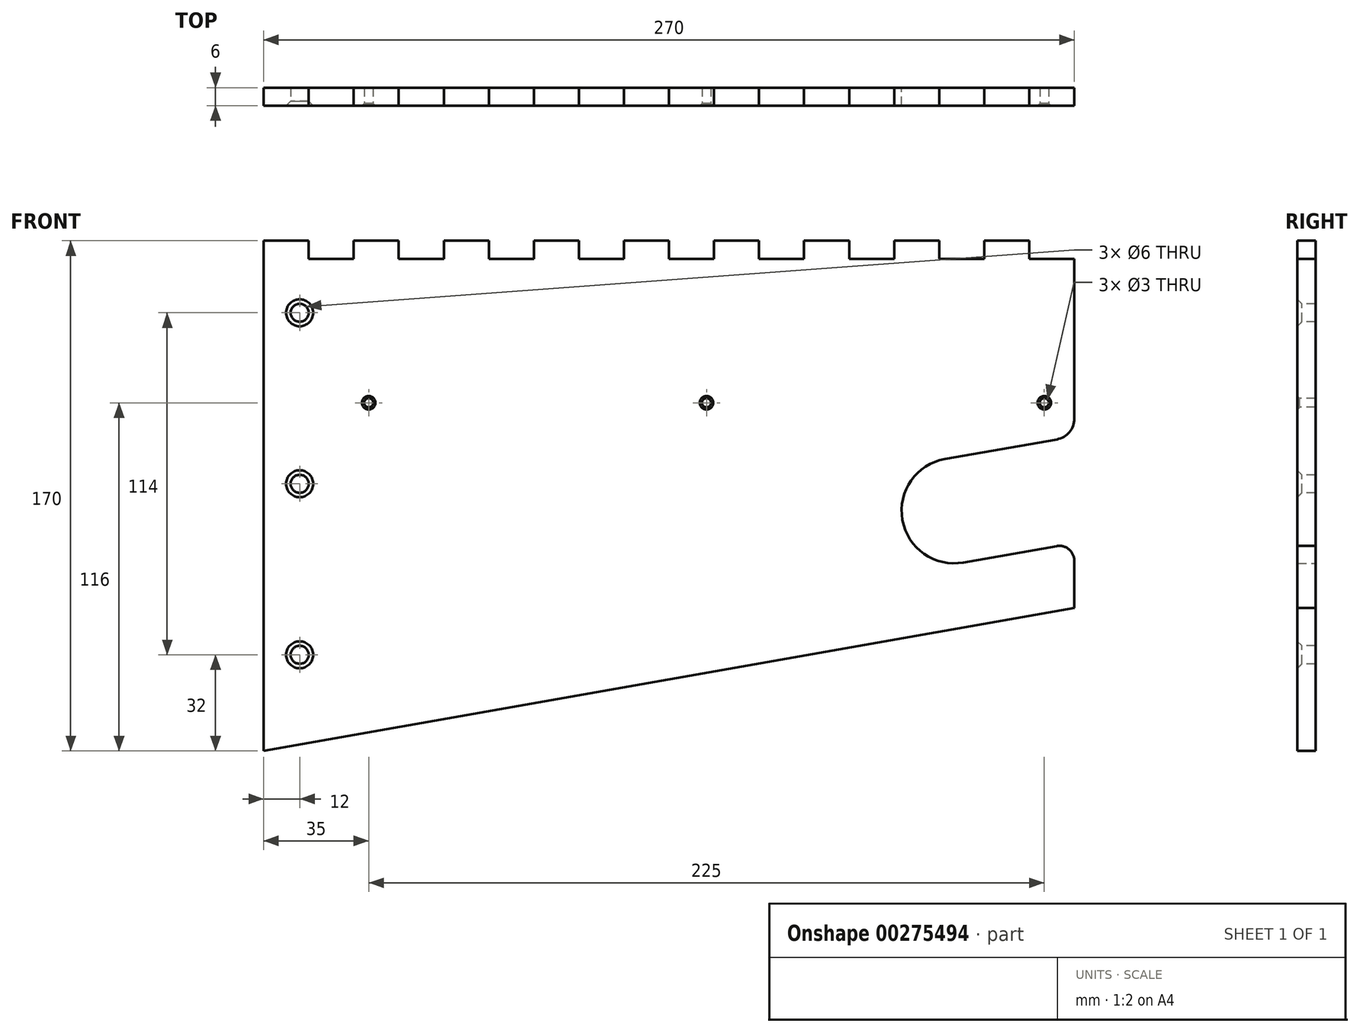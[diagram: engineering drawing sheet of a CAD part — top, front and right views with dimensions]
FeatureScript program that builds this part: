
annotation { "Feature Type Name" : "Feature", "Feature Type Description" : "" }
export const myFeature = defineFeature(function(context is Context, id is Id, definition is map)
    precondition{}
    {
        {
            var Q0;
            Q0=qCreatedBy(makeId("Front.planeOp"),FACE);
            var sketch = newSketch(context, id + "F0", { "sketchPlane" : qUnion([Q0])});
            skLineSegment(sketch, "E0.bottom", {"start": v(0, 0) * mm, "end": v(270, 47.6) * mm});
            skLineSegment(sketch, "E0.top", {"start": v(0, 170) * mm, "end": v(15, 170) * mm});
            skLineSegment(sketch, "E0.left", {"start": v(0, 0) * mm, "end": v(0, 170) * mm});
            skLineSegment(sketch, "E0.right", {"start": v(270, 47.6) * mm, "end": v(270, 63.32) * mm});
            skArc(sketch, "E1", {"start": v(226.96, 97.23) * mm, "mid": v(212.77, 76.96) * mm, "end": v(233.04, 62.77) * mm});
            skLineSegment(sketch, "E2", {"start": v(233.04, 62.77) * mm, "end": v(264.13, 68.25) * mm});
            skLineSegment(sketch, "E3", {"start": v(226.96, 97.23) * mm, "end": v(264.22, 103.8) * mm});
            skLineSegment(sketch, "E4.trimOffspring", {"start": v(270, 110.7) * mm, "end": v(270, 164) * mm});
            skPoint(sketch, "E5.visualSharp", {"position": v(270, 69.28) * mm});
            skArc(sketch, "E5.filletArc", {"start": v(270, 63.32) * mm, "mid": v(268.21, 67.15) * mm, "end": v(264.13, 68.25) * mm});
            skPoint(sketch, "E6.visualSharp", {"position": v(270, 104.82) * mm});
            skArc(sketch, "E6.filletArc", {"start": v(264.22, 103.8) * mm, "mid": v(268.36, 106.2) * mm, "end": v(270, 110.7) * mm});
            skLineSegment(sketch, "E7.top", {"start": v(15, 164) * mm, "end": v(30, 164) * mm});
            skLineSegment(sketch, "E7.left", {"start": v(15, 170) * mm, "end": v(15, 164) * mm});
            skLineSegment(sketch, "E7.right", {"start": v(30, 170) * mm, "end": v(30, 164) * mm});
            skLineSegment(sketch, "E8.1.0.1", {"start": v(45, 170) * mm, "end": v(45, 164) * mm});
            skLineSegment(sketch, "E8.1.0.2", {"start": v(45, 164) * mm, "end": v(60, 164) * mm});
            skLineSegment(sketch, "E8.1.0.3", {"start": v(60, 170) * mm, "end": v(60, 164) * mm});
            skLineSegment(sketch, "E8.2.0.1", {"start": v(75, 170) * mm, "end": v(75, 164) * mm});
            skLineSegment(sketch, "E8.2.0.2", {"start": v(75, 164) * mm, "end": v(90, 164) * mm});
            skLineSegment(sketch, "E8.2.0.3", {"start": v(90, 170) * mm, "end": v(90, 164) * mm});
            skLineSegment(sketch, "E8.3.0.1", {"start": v(105, 170) * mm, "end": v(105, 164) * mm});
            skLineSegment(sketch, "E8.3.0.2", {"start": v(105, 164) * mm, "end": v(120, 164) * mm});
            skLineSegment(sketch, "E8.3.0.3", {"start": v(120, 170) * mm, "end": v(120, 164) * mm});
            skLineSegment(sketch, "E8.4.0.1", {"start": v(135, 170) * mm, "end": v(135, 164) * mm});
            skLineSegment(sketch, "E8.4.0.2", {"start": v(135, 164) * mm, "end": v(150, 164) * mm});
            skLineSegment(sketch, "E8.4.0.3", {"start": v(150, 170) * mm, "end": v(150, 164) * mm});
            skLineSegment(sketch, "E8.5.0.1", {"start": v(165, 170) * mm, "end": v(165, 164) * mm});
            skLineSegment(sketch, "E8.5.0.2", {"start": v(165, 164) * mm, "end": v(180, 164) * mm});
            skLineSegment(sketch, "E8.5.0.3", {"start": v(180, 170) * mm, "end": v(180, 164) * mm});
            skLineSegment(sketch, "E8.6.0.1", {"start": v(195, 170) * mm, "end": v(195, 164) * mm});
            skLineSegment(sketch, "E8.6.0.2", {"start": v(195, 164) * mm, "end": v(210, 164) * mm});
            skLineSegment(sketch, "E8.6.0.3", {"start": v(210, 170) * mm, "end": v(210, 164) * mm});
            skLineSegment(sketch, "E8.7.0.1", {"start": v(225, 170) * mm, "end": v(225, 164) * mm});
            skLineSegment(sketch, "E8.7.0.2", {"start": v(225, 164) * mm, "end": v(240, 164) * mm});
            skLineSegment(sketch, "E8.7.0.3", {"start": v(240, 170) * mm, "end": v(240, 164) * mm});
            skLineSegment(sketch, "E8.8.0.1", {"start": v(255, 170) * mm, "end": v(255, 164) * mm});
            skLineSegment(sketch, "E8.8.0.2", {"start": v(255, 164) * mm, "end": v(270, 164) * mm});
            skLineSegment(sketch, "E8.direction1", {"start": v(30, 170) * mm, "end": v(45, 170) * mm, "construction": true});
            skLineSegment(sketch, "E9.trimOffspring", {"start": v(60, 170) * mm, "end": v(75, 170) * mm});
            skLineSegment(sketch, "E10.trimOffspring", {"start": v(120, 170) * mm, "end": v(135, 170) * mm});
            skLineSegment(sketch, "E11.trimOffspring", {"start": v(150, 170) * mm, "end": v(165, 170) * mm});
            skLineSegment(sketch, "E12.trimOffspring", {"start": v(180, 170) * mm, "end": v(195, 170) * mm});
            skLineSegment(sketch, "E13.trimOffspring", {"start": v(240, 170) * mm, "end": v(255, 170) * mm});
            skLineSegment(sketch, "E14.trimOffspring", {"start": v(210, 170) * mm, "end": v(225, 170) * mm});
            skLineSegment(sketch, "E15.trimOffspring", {"start": v(90, 170) * mm, "end": v(105, 170) * mm});
            skLineSegment(sketch, "E16.trimOffspring", {"start": v(30, 170) * mm, "end": v(45, 170) * mm});
            skSolve(sketch);
        }
        {
            var Q0;
            Q0=makeQuery(id+"F0.imprint","IMPRINT",FACE,{"disambiguationData":[TD([[makeQuery(id+"F0.imprint","IMPRINT",EDGE,{"derivedFrom":sQuery(id+"F0.wireOp",EDGE,"E0.bottom")}),1.0]])]});
            extrude(context, id + "F1", {"entities" : qUnion([Q0]), "depth" : 6 * mm});
        }
        {
            var Q0;
            Q0=makeQuery(id+"F1.opExtrude","CAP_FACE",FACE,{"disambiguationData":[OSD([sQuery(id+"F0.wireOp",EDGE,"E0.bottom"),sQuery(id+"F0.wireOp",EDGE,"E0.top"),sQuery(id+"F0.wireOp",EDGE,"E0.left"),sQuery(id+"F0.wireOp",EDGE,"E0.right"),sQuery(id+"F0.wireOp",EDGE,"E1"),sQuery(id+"F0.wireOp",EDGE,"E2"),sQuery(id+"F0.wireOp",EDGE,"E3"),sQuery(id+"F0.wireOp",EDGE,"E4.trimOffspring"),sQuery(id+"F0.wireOp",EDGE,"E5.filletArc"),sQuery(id+"F0.wireOp",EDGE,"E6.filletArc"),sQuery(id+"F0.wireOp",EDGE,"E7.top"),sQuery(id+"F0.wireOp",EDGE,"E7.left"),sQuery(id+"F0.wireOp",EDGE,"E7.right"),sQuery(id+"F0.wireOp",EDGE,"E8.1.0.1"),sQuery(id+"F0.wireOp",EDGE,"E8.1.0.2"),sQuery(id+"F0.wireOp",EDGE,"E8.1.0.3"),sQuery(id+"F0.wireOp",EDGE,"E8.2.0.1"),sQuery(id+"F0.wireOp",EDGE,"E8.2.0.2"),sQuery(id+"F0.wireOp",EDGE,"E8.2.0.3"),sQuery(id+"F0.wireOp",EDGE,"E8.3.0.1"),sQuery(id+"F0.wireOp",EDGE,"E8.3.0.2"),sQuery(id+"F0.wireOp",EDGE,"E8.3.0.3"),sQuery(id+"F0.wireOp",EDGE,"E8.4.0.1"),sQuery(id+"F0.wireOp",EDGE,"E8.4.0.2"),sQuery(id+"F0.wireOp",EDGE,"E8.4.0.3"),sQuery(id+"F0.wireOp",EDGE,"E8.5.0.1"),sQuery(id+"F0.wireOp",EDGE,"E8.5.0.2"),sQuery(id+"F0.wireOp",EDGE,"E8.5.0.3"),sQuery(id+"F0.wireOp",EDGE,"E8.6.0.1"),sQuery(id+"F0.wireOp",EDGE,"E8.6.0.2"),sQuery(id+"F0.wireOp",EDGE,"E8.6.0.3"),sQuery(id+"F0.wireOp",EDGE,"E8.7.0.1"),sQuery(id+"F0.wireOp",EDGE,"E8.7.0.2"),sQuery(id+"F0.wireOp",EDGE,"E8.7.0.3"),sQuery(id+"F0.wireOp",EDGE,"E8.8.0.1"),sQuery(id+"F0.wireOp",EDGE,"E8.8.0.2"),sQuery(id+"F0.wireOp",EDGE,"E9.trimOffspring"),sQuery(id+"F0.wireOp",EDGE,"E10.trimOffspring"),sQuery(id+"F0.wireOp",EDGE,"E11.trimOffspring"),sQuery(id+"F0.wireOp",EDGE,"E12.trimOffspring"),sQuery(id+"F0.wireOp",EDGE,"E13.trimOffspring"),sQuery(id+"F0.wireOp",EDGE,"E14.trimOffspring"),sQuery(id+"F0.wireOp",EDGE,"E15.trimOffspring"),sQuery(id+"F0.wireOp",EDGE,"E16.trimOffspring")])],"isStart":false});
            var sketch = newSketch(context, id + "F2", { "sketchPlane" : qUnion([Q0])});
            skPoint(sketch, "E17", {"position": v(12, 146) * mm});
            skPoint(sketch, "E18", {"position": v(12, 89) * mm});
            skPoint(sketch, "E19", {"position": v(12, 32) * mm});
            skSolve(sketch);
        }
        {
            var Q0;
            Q0=sQuery(id+"F2.wireOp",VERTEX,"E17");
            var Q1;
            Q1=sQuery(id+"F2.wireOp",VERTEX,"E18");
            var Q2;
            Q2=sQuery(id+"F2.wireOp",VERTEX,"E19");
            var Q3;
            Q3=makeQuery(id+"F1.opExtrude","SWEPT_BODY",BODY,{"disambiguationData":[OSD([sQuery(id+"F0.wireOp",EDGE,"E0.bottom"),sQuery(id+"F0.wireOp",EDGE,"E0.top"),sQuery(id+"F0.wireOp",EDGE,"E0.left"),sQuery(id+"F0.wireOp",EDGE,"E0.right"),sQuery(id+"F0.wireOp",EDGE,"E1"),sQuery(id+"F0.wireOp",EDGE,"E2"),sQuery(id+"F0.wireOp",EDGE,"E3"),sQuery(id+"F0.wireOp",EDGE,"E4.trimOffspring"),sQuery(id+"F0.wireOp",EDGE,"E5.filletArc"),sQuery(id+"F0.wireOp",EDGE,"E6.filletArc"),sQuery(id+"F0.wireOp",EDGE,"E7.top"),sQuery(id+"F0.wireOp",EDGE,"E7.left"),sQuery(id+"F0.wireOp",EDGE,"E7.right"),sQuery(id+"F0.wireOp",EDGE,"E8.1.0.1"),sQuery(id+"F0.wireOp",EDGE,"E8.1.0.2"),sQuery(id+"F0.wireOp",EDGE,"E8.1.0.3"),sQuery(id+"F0.wireOp",EDGE,"E8.2.0.1"),sQuery(id+"F0.wireOp",EDGE,"E8.2.0.2"),sQuery(id+"F0.wireOp",EDGE,"E8.2.0.3"),sQuery(id+"F0.wireOp",EDGE,"E8.3.0.1"),sQuery(id+"F0.wireOp",EDGE,"E8.3.0.2"),sQuery(id+"F0.wireOp",EDGE,"E8.3.0.3"),sQuery(id+"F0.wireOp",EDGE,"E8.4.0.1"),sQuery(id+"F0.wireOp",EDGE,"E8.4.0.2"),sQuery(id+"F0.wireOp",EDGE,"E8.4.0.3"),sQuery(id+"F0.wireOp",EDGE,"E8.5.0.1"),sQuery(id+"F0.wireOp",EDGE,"E8.5.0.2"),sQuery(id+"F0.wireOp",EDGE,"E8.5.0.3"),sQuery(id+"F0.wireOp",EDGE,"E8.6.0.1"),sQuery(id+"F0.wireOp",EDGE,"E8.6.0.2"),sQuery(id+"F0.wireOp",EDGE,"E8.6.0.3"),sQuery(id+"F0.wireOp",EDGE,"E8.7.0.1"),sQuery(id+"F0.wireOp",EDGE,"E8.7.0.2"),sQuery(id+"F0.wireOp",EDGE,"E8.7.0.3"),sQuery(id+"F0.wireOp",EDGE,"E8.8.0.1"),sQuery(id+"F0.wireOp",EDGE,"E8.8.0.2"),sQuery(id+"F0.wireOp",EDGE,"E9.trimOffspring"),sQuery(id+"F0.wireOp",EDGE,"E10.trimOffspring"),sQuery(id+"F0.wireOp",EDGE,"E11.trimOffspring"),sQuery(id+"F0.wireOp",EDGE,"E12.trimOffspring"),sQuery(id+"F0.wireOp",EDGE,"E13.trimOffspring"),sQuery(id+"F0.wireOp",EDGE,"E14.trimOffspring"),sQuery(id+"F0.wireOp",EDGE,"E15.trimOffspring"),sQuery(id+"F0.wireOp",EDGE,"E16.trimOffspring")])]});
            hole(context, id + "F3", {"style" : HoleStyle.C_SINK, "endStyle" : HoleEndStyle.THROUGH, "standardTappedOrClearance" : lookupTablePath({ "standard" : "ISO", "size" : "6", "type" : "Drilled" }), "standardBlindInLast" : lookupTablePath({ "standard" : "ISO", "size" : "6", "type" : "Drilled" }), "holeDiameter" : 6 * mm, "cSinkDiameter" : 9 * mm, "cSinkAngle" : 90 * degree, "tappedDepth" : 12 * mm, "tapClearance" : 3, "locations" : qUnion([Q0, Q1, Q2]), "scope" : qUnion([Q3])});
        }
        {
            var Q0;
            Q0=makeQuery(id+"F1.opExtrude","CAP_FACE",FACE,{"disambiguationData":[OSD([sQuery(id+"F0.wireOp",EDGE,"E0.bottom"),sQuery(id+"F0.wireOp",EDGE,"E0.top"),sQuery(id+"F0.wireOp",EDGE,"E0.left"),sQuery(id+"F0.wireOp",EDGE,"E0.right"),sQuery(id+"F0.wireOp",EDGE,"E1"),sQuery(id+"F0.wireOp",EDGE,"E2"),sQuery(id+"F0.wireOp",EDGE,"E3"),sQuery(id+"F0.wireOp",EDGE,"E4.trimOffspring"),sQuery(id+"F0.wireOp",EDGE,"E5.filletArc"),sQuery(id+"F0.wireOp",EDGE,"E6.filletArc"),sQuery(id+"F0.wireOp",EDGE,"E7.top"),sQuery(id+"F0.wireOp",EDGE,"E7.left"),sQuery(id+"F0.wireOp",EDGE,"E7.right"),sQuery(id+"F0.wireOp",EDGE,"E8.1.0.1"),sQuery(id+"F0.wireOp",EDGE,"E8.1.0.2"),sQuery(id+"F0.wireOp",EDGE,"E8.1.0.3"),sQuery(id+"F0.wireOp",EDGE,"E8.2.0.1"),sQuery(id+"F0.wireOp",EDGE,"E8.2.0.2"),sQuery(id+"F0.wireOp",EDGE,"E8.2.0.3"),sQuery(id+"F0.wireOp",EDGE,"E8.3.0.1"),sQuery(id+"F0.wireOp",EDGE,"E8.3.0.2"),sQuery(id+"F0.wireOp",EDGE,"E8.3.0.3"),sQuery(id+"F0.wireOp",EDGE,"E8.4.0.1"),sQuery(id+"F0.wireOp",EDGE,"E8.4.0.2"),sQuery(id+"F0.wireOp",EDGE,"E8.4.0.3"),sQuery(id+"F0.wireOp",EDGE,"E8.5.0.1"),sQuery(id+"F0.wireOp",EDGE,"E8.5.0.2"),sQuery(id+"F0.wireOp",EDGE,"E8.5.0.3"),sQuery(id+"F0.wireOp",EDGE,"E8.6.0.1"),sQuery(id+"F0.wireOp",EDGE,"E8.6.0.2"),sQuery(id+"F0.wireOp",EDGE,"E8.6.0.3"),sQuery(id+"F0.wireOp",EDGE,"E8.7.0.1"),sQuery(id+"F0.wireOp",EDGE,"E8.7.0.2"),sQuery(id+"F0.wireOp",EDGE,"E8.7.0.3"),sQuery(id+"F0.wireOp",EDGE,"E8.8.0.1"),sQuery(id+"F0.wireOp",EDGE,"E8.8.0.2"),sQuery(id+"F0.wireOp",EDGE,"E9.trimOffspring"),sQuery(id+"F0.wireOp",EDGE,"E10.trimOffspring"),sQuery(id+"F0.wireOp",EDGE,"E11.trimOffspring"),sQuery(id+"F0.wireOp",EDGE,"E12.trimOffspring"),sQuery(id+"F0.wireOp",EDGE,"E13.trimOffspring"),sQuery(id+"F0.wireOp",EDGE,"E14.trimOffspring"),sQuery(id+"F0.wireOp",EDGE,"E15.trimOffspring"),sQuery(id+"F0.wireOp",EDGE,"E16.trimOffspring")])],"isStart":false});
            var sketch = newSketch(context, id + "F4", { "sketchPlane" : qUnion([Q0])});
            skPoint(sketch, "E20", {"position": v(35, 116) * mm});
            skPoint(sketch, "E21", {"position": v(147.5, 116) * mm});
            skPoint(sketch, "E22", {"position": v(260, 116) * mm});
            skSolve(sketch);
        }
        {
            var Q0;
            Q0=sQuery(id+"F4.wireOp",VERTEX,"E20");
            var Q1;
            Q1=sQuery(id+"F4.wireOp",VERTEX,"E21");
            var Q2;
            Q2=sQuery(id+"F4.wireOp",VERTEX,"E22");
            var Q3;
            Q3=makeQuery(id+"F1.opExtrude","SWEPT_BODY",BODY,{"disambiguationData":[OSD([sQuery(id+"F0.wireOp",EDGE,"E0.bottom"),sQuery(id+"F0.wireOp",EDGE,"E0.top"),sQuery(id+"F0.wireOp",EDGE,"E0.left"),sQuery(id+"F0.wireOp",EDGE,"E0.right"),sQuery(id+"F0.wireOp",EDGE,"E1"),sQuery(id+"F0.wireOp",EDGE,"E2"),sQuery(id+"F0.wireOp",EDGE,"E3"),sQuery(id+"F0.wireOp",EDGE,"E4.trimOffspring"),sQuery(id+"F0.wireOp",EDGE,"E5.filletArc"),sQuery(id+"F0.wireOp",EDGE,"E6.filletArc"),sQuery(id+"F0.wireOp",EDGE,"E7.top"),sQuery(id+"F0.wireOp",EDGE,"E7.left"),sQuery(id+"F0.wireOp",EDGE,"E7.right"),sQuery(id+"F0.wireOp",EDGE,"E8.1.0.1"),sQuery(id+"F0.wireOp",EDGE,"E8.1.0.2"),sQuery(id+"F0.wireOp",EDGE,"E8.1.0.3"),sQuery(id+"F0.wireOp",EDGE,"E8.2.0.1"),sQuery(id+"F0.wireOp",EDGE,"E8.2.0.2"),sQuery(id+"F0.wireOp",EDGE,"E8.2.0.3"),sQuery(id+"F0.wireOp",EDGE,"E8.3.0.1"),sQuery(id+"F0.wireOp",EDGE,"E8.3.0.2"),sQuery(id+"F0.wireOp",EDGE,"E8.3.0.3"),sQuery(id+"F0.wireOp",EDGE,"E8.4.0.1"),sQuery(id+"F0.wireOp",EDGE,"E8.4.0.2"),sQuery(id+"F0.wireOp",EDGE,"E8.4.0.3"),sQuery(id+"F0.wireOp",EDGE,"E8.5.0.1"),sQuery(id+"F0.wireOp",EDGE,"E8.5.0.2"),sQuery(id+"F0.wireOp",EDGE,"E8.5.0.3"),sQuery(id+"F0.wireOp",EDGE,"E8.6.0.1"),sQuery(id+"F0.wireOp",EDGE,"E8.6.0.2"),sQuery(id+"F0.wireOp",EDGE,"E8.6.0.3"),sQuery(id+"F0.wireOp",EDGE,"E8.7.0.1"),sQuery(id+"F0.wireOp",EDGE,"E8.7.0.2"),sQuery(id+"F0.wireOp",EDGE,"E8.7.0.3"),sQuery(id+"F0.wireOp",EDGE,"E8.8.0.1"),sQuery(id+"F0.wireOp",EDGE,"E8.8.0.2"),sQuery(id+"F0.wireOp",EDGE,"E9.trimOffspring"),sQuery(id+"F0.wireOp",EDGE,"E10.trimOffspring"),sQuery(id+"F0.wireOp",EDGE,"E11.trimOffspring"),sQuery(id+"F0.wireOp",EDGE,"E12.trimOffspring"),sQuery(id+"F0.wireOp",EDGE,"E13.trimOffspring"),sQuery(id+"F0.wireOp",EDGE,"E14.trimOffspring"),sQuery(id+"F0.wireOp",EDGE,"E15.trimOffspring"),sQuery(id+"F0.wireOp",EDGE,"E16.trimOffspring")])]});
            hole(context, id + "F5", {"style" : HoleStyle.C_SINK, "endStyle" : HoleEndStyle.THROUGH, "holeDiameter" : 3 * mm, "cSinkDiameter" : 4.5 * mm, "cSinkAngle" : 90 * degree, "tappedDepth" : 12 * mm, "tapClearance" : 3, "locations" : qUnion([Q0, Q1, Q2]), "scope" : qUnion([Q3])});
        }
    });
